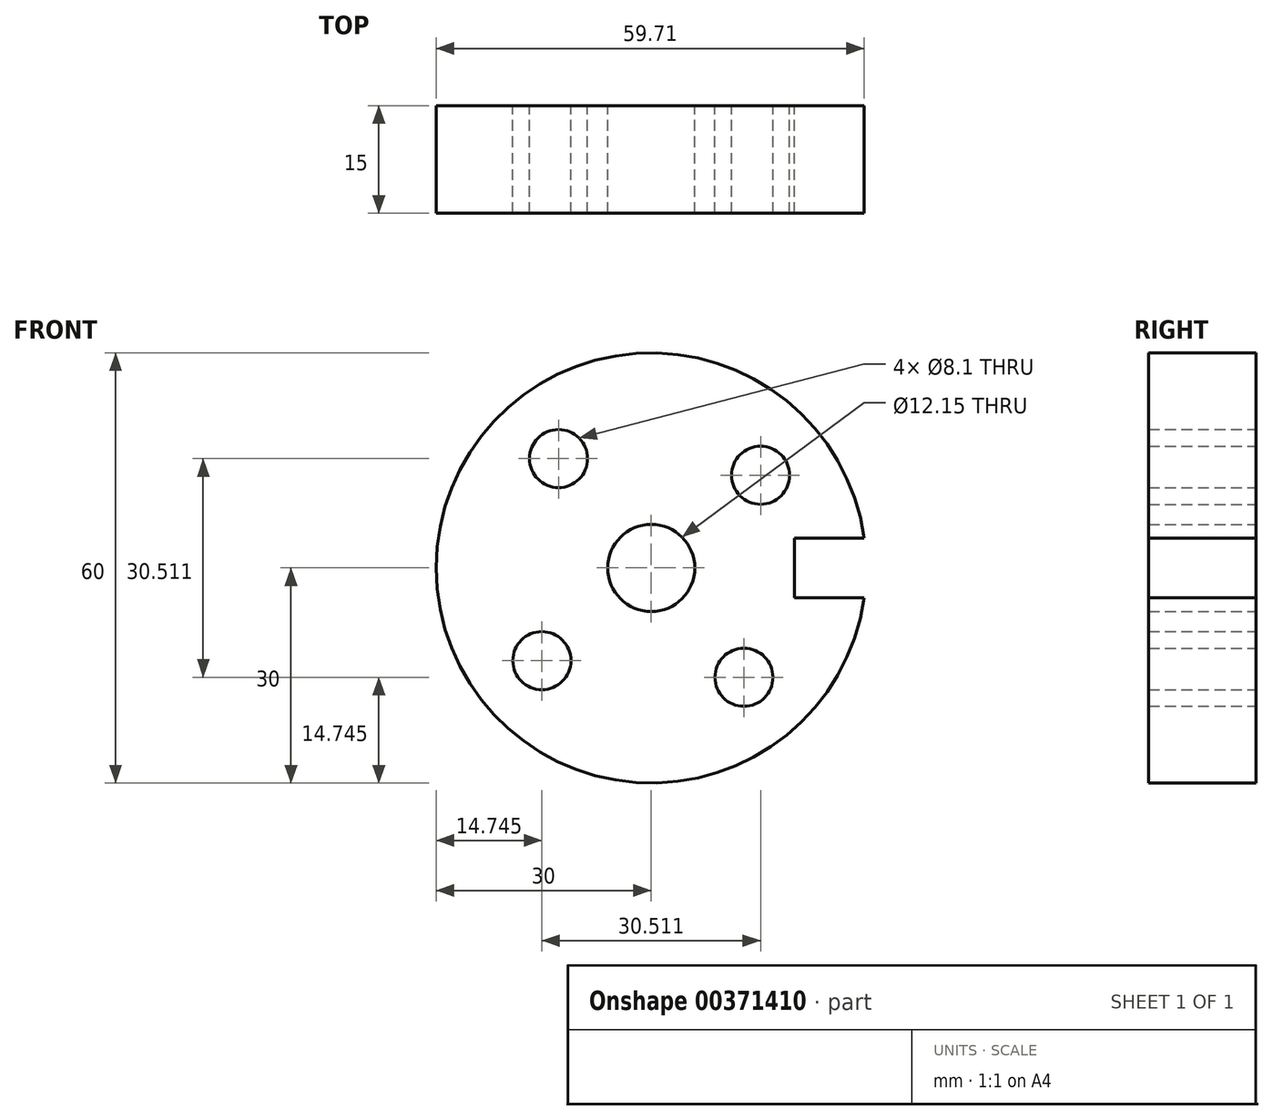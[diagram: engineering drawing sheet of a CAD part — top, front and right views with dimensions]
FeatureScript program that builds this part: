
annotation { "Feature Type Name" : "Feature", "Feature Type Description" : "" }
export const myFeature = defineFeature(function(context is Context, id is Id, definition is map)
    precondition{}
    {
        {
            var Q0;
            Q0=qCreatedBy(makeId("Front.planeOp"),FACE);
            var sketch = newSketch(context, id + "F0", { "sketchPlane" : qUnion([Q0])});
            skArc(sketch, "E0", {"start": v(29.7, 4.18) * mm, "mid": v(-30, 0) * mm, "end": v(29.7, -4.18) * mm});
            skCircle(sketch, "E1", {"center": v(-12.93, 15.26) * mm, "radius": 4.05 * mm});
            skCircle(sketch, "E2", {"center": v(0, 0) * mm, "radius": 6.08 * mm});
            skCircle(sketch, "E3.1.0", {"center": v(-15.26, -12.93) * mm, "radius": 4.05 * mm});
            skCircle(sketch, "E3.2.0", {"center": v(12.93, -15.26) * mm, "radius": 4.05 * mm});
            skCircle(sketch, "E3.3.0", {"center": v(15.26, 12.93) * mm, "radius": 4.05 * mm});
            skLineSegment(sketch, "E4", {"start": v(29.7, 4.18) * mm, "end": v(20, 4.17) * mm});
            skLineSegment(sketch, "E5", {"start": v(20, 4.17) * mm, "end": v(20, -4.18) * mm});
            skLineSegment(sketch, "E6", {"start": v(20, -4.18) * mm, "end": v(29.7, -4.17) * mm});
            skSolve(sketch);
        }
        {
            var Q0;
            Q0 = qSketchRegion(id + "F0", true);
            extrude(context, id + "F1", {"entities" : qUnion([Q0]), "depth" : 15 * mm});
        }
    });
